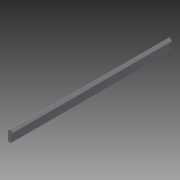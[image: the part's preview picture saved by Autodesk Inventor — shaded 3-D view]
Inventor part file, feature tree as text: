
AUTODESK INVENTOR PART (.ipt)
format: ipt  version: 2016 SP1 (Build 200210100, 210)  size: 99,840 bytes
history: native  units: in
note: dims shown in document units (in); Inventor stores cm internally (conversion verified against a paired STEP export)
features: fillet x1, other x1, imported_body x1
ambient origin geometry x8: Origin, YZ Plane, XZ Plane, XY Plane, X Axis, Y Axis, Z Axis, Center Point
bodies: Body1 (feature_tree)
feature tree (3):
  fillet  "Fillet1"  [1 undecoded]
  other  "BWC-T3-11"
  imported_body  "Base1"
note: 1 required parameter value undecoded (feature->parameter linkage not recoverable at this tier; creation-order binding heuristic only, values carry confidence <= 0.55)
